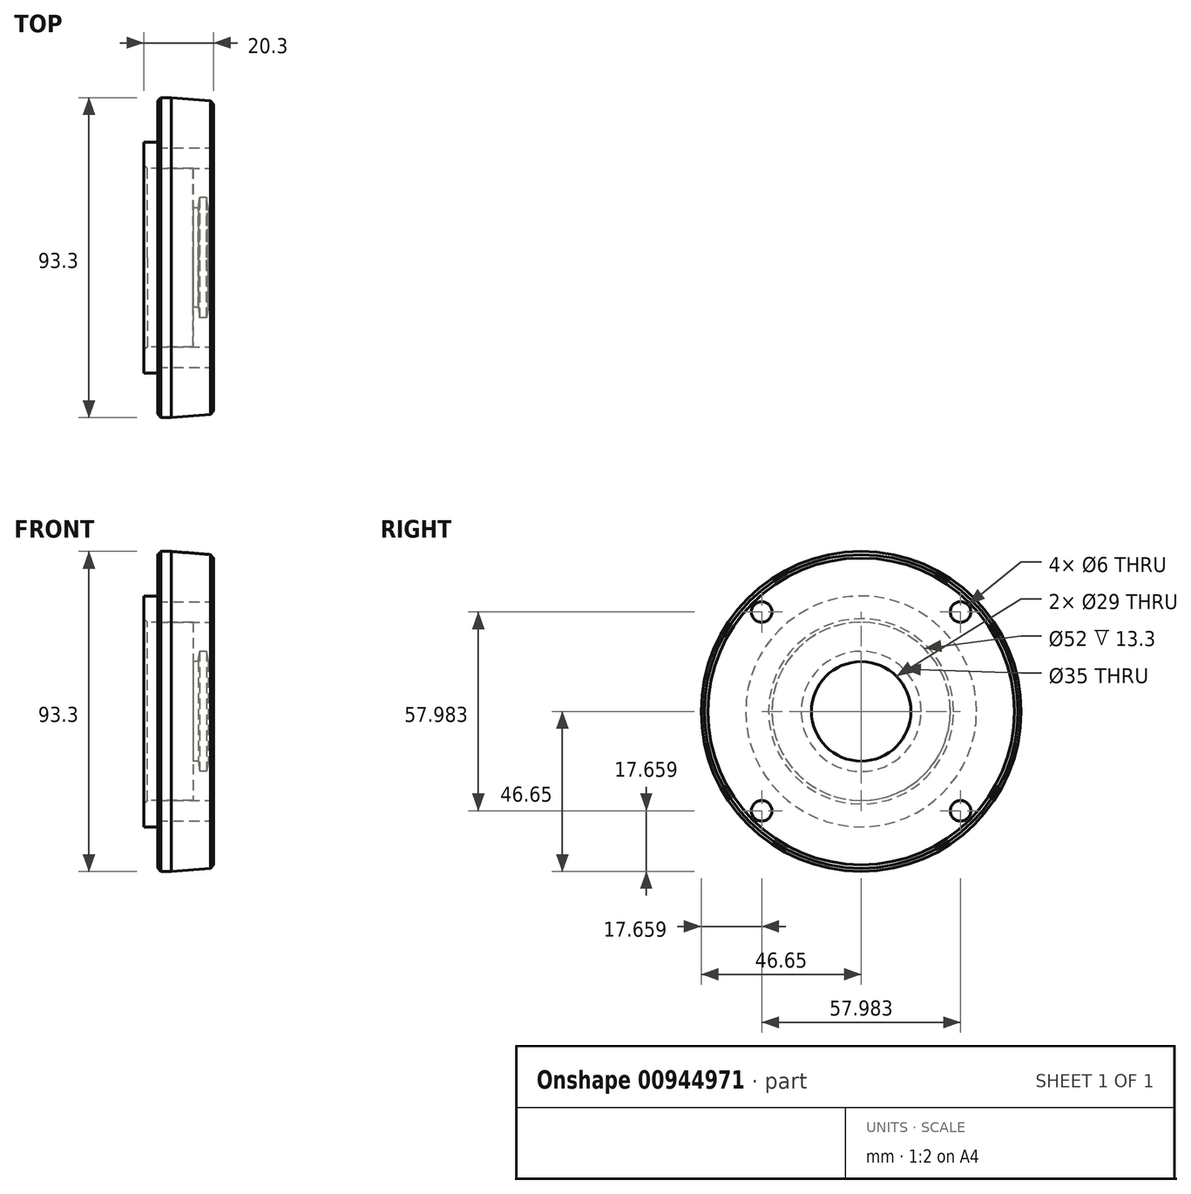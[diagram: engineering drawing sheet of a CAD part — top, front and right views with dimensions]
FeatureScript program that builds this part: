
annotation { "Feature Type Name" : "Feature", "Feature Type Description" : "" }
export const myFeature = defineFeature(function(context is Context, id is Id, definition is map)
    precondition{}
    {
        {
            var Q0;
            Q0=qCreatedBy(makeId("Front.planeOp"),FACE);
            var sketch = newSketch(context, id + "F0", { "sketchPlane" : qUnion([Q0])});
            skLineSegment(sketch, "E0", {"start": v(0, 33.65) * mm, "end": v(0, 46.65) * mm});
            skLineSegment(sketch, "E1", {"start": v(0, 46.65) * mm, "end": v(4, 46.65) * mm});
            skLineSegment(sketch, "E2", {"start": v(16.3, 45.63) * mm, "end": v(4, 46.65) * mm});
            skLineSegment(sketch, "E3", {"start": v(0, 0) * mm, "end": v(36.35, 0) * mm});
            skLineSegment(sketch, "E4", {"start": v(0, 33.65) * mm, "end": v(-4, 33.65) * mm});
            skLineSegment(sketch, "E5", {"start": v(-4, 33.65) * mm, "end": v(-4, 26) * mm});
            skLineSegment(sketch, "E6", {"start": v(0, 26) * mm, "end": v(-4, 26) * mm});
            skLineSegment(sketch, "E7", {"start": v(0, 0) * mm, "end": v(16, 0) * mm});
            skPoint(sketch, "E8.orphan", {"position": v(20, 0) * mm});
            skLineSegment(sketch, "E9", {"start": v(10.3, 26) * mm, "end": v(10.3, 14.5) * mm});
            skLineSegment(sketch, "E10", {"start": v(16.3, 14.5) * mm, "end": v(16.3, 45.63) * mm});
            skLineSegment(sketch, "E11", {"start": v(0, 26) * mm, "end": v(10.3, 26) * mm});
            skLineSegment(sketch, "E12", {"start": v(16.3, 14.5) * mm, "end": v(14.8, 14.5) * mm});
            skLineSegment(sketch, "E13", {"start": v(10.3, 14.5) * mm, "end": v(11.8, 14.5) * mm});
            skLineSegment(sketch, "E14", {"start": v(13.3, 17.5) * mm, "end": v(14.3, 17.5) * mm});
            skLineSegment(sketch, "E15", {"start": v(14.3, 17.5) * mm, "end": v(12.3, 17.5) * mm});
            skLineSegment(sketch, "E16", {"start": v(12.3, 17.5) * mm, "end": v(11.8, 14.5) * mm});
            skLineSegment(sketch, "E17", {"start": v(14.8, 14.5) * mm, "end": v(14.3, 17.5) * mm});
            skSolve(sketch);
        }
        {
            var Q0;
            Q0=makeQuery(id+"F0.imprint","IMPRINT",FACE,{"disambiguationData":[TD([[makeQuery(id+"F0.imprint","IMPRINT",EDGE,{"derivedFrom":sQuery(id+"F0.wireOp",EDGE,"E0")}),-1.0]])]});
            var Q1;
            Q1=sQuery(id+"F0.wireOp",EDGE,"E3");
            revolve(context, id + "F1", {"surfaceOperationType" : NewSurfaceOperationType.NEW, "entities" : qUnion([Q0]), "axis" : qUnion([Q1]), "revolveType" : RevolveType.FULL});
        }
        {
            var Q0;
            Q0=makeQuery(id+"F1.opRevolve","SWEPT_FACE",FACE,{"disambiguationData":[OSD([sQuery(id+"F0.wireOp",EDGE,"E10")])]});
            var sketch = newSketch(context, id + "F2", { "sketchPlane" : qUnion([Q0])});
            skCircle(sketch, "E18", {"center": v(29, 29) * mm, "radius": 3 * mm});
            skCircle(sketch, "E19", {"center": v(29, -29) * mm, "radius": 3 * mm});
            skCircle(sketch, "E20", {"center": v(-29, 29) * mm, "radius": 3 * mm});
            skCircle(sketch, "E21", {"center": v(-29, -29) * mm, "radius": 3 * mm});
            skSolve(sketch);
        }
        {
            var Q0;
            Q0 = qSketchRegion(id + "F2", true);
            extrude(context, id + "F3", {"entities" : qUnion([Q0]), "operationType" : NewBodyOperationType.REMOVE, "oppositeDirection" : true, "depth" : 25 * mm, "offsetDistance" : 25 * mm});
        }
        {
            var Q0;
            Q0=makeQuery(id+"F1.opRevolve","SWEPT_EDGE",EDGE,{"disambiguationData":[OSD([sQuery(id+"F0.wireOp",EDGE,"E2"),sQuery(id+"F0.wireOp",EDGE,"E10")])]});
            var Q1;
            Q1=makeQuery(id+"F1.opRevolve","SWEPT_EDGE",EDGE,{"disambiguationData":[OSD([sQuery(id+"F0.wireOp",EDGE,"E0"),sQuery(id+"F0.wireOp",EDGE,"E1")])]});
            chamfer(context, id + "F4", {"entities" : qUnion([Q0, Q1]), "width" : 1 * mm, "tangentPropagation" : true});
        }
        {
            var Q0;
            Q0=makeQuery(id+"F1.opRevolve","SWEPT_EDGE",EDGE,{"disambiguationData":[OSD([sQuery(id+"F0.wireOp",EDGE,"E5"),sQuery(id+"F0.wireOp",EDGE,"E6")])]});
            chamfer(context, id + "F5", {"entities" : qUnion([Q0]), "width" : 1 * mm, "tangentPropagation" : true});
        }
    });
